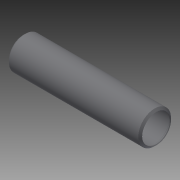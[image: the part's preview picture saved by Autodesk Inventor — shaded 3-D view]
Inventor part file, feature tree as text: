
AUTODESK INVENTOR PART (.ipt)
format: ipt  version: 2014 (Build 180170000, 170)  size: 128,000 bytes
history: native  units: in
note: dims shown in document units (in); Inventor stores cm internally (conversion verified against a paired STEP export)
features: other x56, revolve x1, sketch x1
ambient origin geometry x8: Origin, YZ Plane, XZ Plane, XY Plane, X Axis, Y Axis, Z Axis, Center Point
bodies: Solid1 (feature_tree)
feature tree (58):
  revolve  "Revolution1"  [1 undecoded]
  other  "o1_XY"
  other  "o1_YZ"
  other  "o1_ZX"
  other  "o1_X"
  other  "o1_Y"
  other  "o1_Z"
  other  "o1_Center"
  other  "o2_XY"
  other  "o2_YZ"
  other  "o2_ZX"
  other  "o2_X"
  other  "o2_Y"
  other  "o2_Z"
  other  "o2_Center"
  other  "t1_XY"
  other  "t1_YZ"
  other  "t1_ZX"
  other  "t1_X"
  other  "t1_Y"
  other  "t1_Z"
  other  "t1_Center"
  other  "t2_XY"
  other  "t2_YZ"
  other  "t2_ZX"
  other  "t2_X"
  other  "t2_Y"
  other  "t2_Z"
  other  "t2_Center"
  other  "t3_XY"
  other  "t3_YZ"
  other  "t3_ZX"
  other  "t3_X"
  other  "t3_Y"
  other  "t3_Z"
  other  "t3_Center"
  other  "t4_XY"
  other  "t4_YZ"
  other  "t4_ZX"
  other  "t4_X"
  other  "t4_Y"
  other  "t4_Z"
  other  "t4_Center"
  other  "tube1_XY"
  other  "tube1_YZ"
  other  "tube1_ZX"
  other  "tube1_X"
  other  "tube1_Y"
  other  "tube1_Z"
  other  "tube1_Center"
  other  "tube2_XY"
  other  "tube2_YZ"
  other  "tube2_ZX"
  other  "tube2_X"
  other  "tube2_Y"
  other  "tube2_Z"
  other  "tube2_Center"
  sketch  "Sketch_5"  dims[d0=360.0deg]
note: 1 required parameter value undecoded (feature->parameter linkage not recoverable at this tier; creation-order binding heuristic only, values carry confidence <= 0.55)
